# Revit family: ATAG_CV_ketel_Q25_en_Q38_combi
name_source: partatom
category: Mechanical Equipment
revit_build: Autodesk Revit 2014 (Build: 20130308_1515(x64)
units: mm (PartAtom-declared; Revit-internal decimal feet)

## types (2) — shared parameters
BCB_I BaseKeynote = 56.10.10.13.01
BCB_I Beschermingsgraad vlgs. EN 60529 = IPX0D
BCB_I Gaskeur HR Top = HR Top
BCB_I Gaskeur HRww_gaskeurlabel hoog rendement warm water = HR
BCB_I Gaskeur NZ_gaskeurlabel naverwarming zon = NZ
BCB_I Gaskeur SV_gaskeurlabel schone verbranding = SV
BCB_I Max tapwater temperatuur = 60 °C
BCB_V Aansluitdiameter CVr = 28 mm
BCB_V Aansluitdiameter CVv = 28 mm
BCB_V Aansluitdiameter KW = 15 mm
BCB_V Aansluitdiameter WW = 15 mm
BCB_V Aansluitdiameter condensafvoer = 22 mm
BCB_V Aansluitdiameter expansievat = 22 mm
BCB_V Aansluitdiameter gas = 15 mm
BCB_V Aansluitdiameter luchttoevoer = 80 mm  [stored 0.262467 ft]
BCB_V Aansluitdiameter rookgasafvoer = 80 mm  [stored 0.262467 ft]
BCB_V Luchtinlaat_materiaal = BE Kunststof_zwart
BCB_c1 Debiet = 0 CFM
BCB_c1 Omschrijving = c1_Rookgasafvoer
BCB_c1 Straal = 40 mm  [stored 0.131234 ft]
BCB_c10 Omschrijving = c10_Expansievat
BCB_c10 Straal = 11 mm  [stored 0.0360892 ft]
BCB_c2 Omschrijving = c2_Elektrische voeding
BCB_c3 Debiet = 0.0000 L/s
BCB_c3 Energie_inhoud gas = 0 kWh
BCB_c3 Omschrijving = c3_Gasaansluiting
BCB_c3 Straal = 8 mm  [stored 0.0262467 ft]
BCB_c3 Vermogen = 0 kW
BCB_c4 Omschrijving = c4_CV-toevoer
BCB_c4 Straal = 14 mm  [stored 0.0459318 ft]
BCB_c5 Omschrijving = c5_CV-retour
BCB_c5 Straal = 14 mm  [stored 0.0459318 ft]
BCB_c6 Omschrijving = c6_Condensafvoer
BCB_c6 Straal = 11 mm  [stored 0.0360892 ft]
BCB_c7 Debiet = 0 CFM
BCB_c7 Omschrijving = c7_Luchttoevoer
BCB_c7 Straal = 40 mm  [stored 0.131234 ft]
BCB_c8 Debiet = 0.0000 L/s
BCB_c8 Omschrijving = c8_Aansluiting WW
BCB_c8 Straal = 8 mm  [stored 0.0262467 ft]
BCB_c9 Omschrijving = c9_Aansluiting KW
BCB_c9 Straal = 8 mm  [stored 0.0262467 ft]
Default Elevation = 1000 mm  [stored 3.28084 ft]
GTIN-14 = -
IFC_versie = 2x3
IfcExportAs = IfcGasTerminalType
IfcExportType = gasappliance
Manufacturer = ATAG
Model = Q-serie
NL_E Aantal polen = 1
NL_E Arbeidsfactor = 1
NL_E Belastingsklasse = Other
NL_E Belastingssubklasse motor = No
NL_E Schijnbaar vermogen = 0 VA
NL_E Spanning = 230 V
NL_E Vermogen = 0 W
NL_G Breedte = 840 mm
NL_G Diepte = 385 mm  [stored 1.26312 ft]
NL_G Hoogte = 680 mm  [stored 2.23097 ft]
NL_I Bestelcode = -
NL_M Debiet = 0 CFM
NL_P FBW = 0.5
Type Comments = wandketel
ZZ_Z Aansluiting CV_geen accessoire = NL_M Accessoires aansluitingen CV : Geen
ZZ_Z Aansluiting CVr_X coördinaat = -135 mm
ZZ_Z Aansluiting CVr_type accessoire = NL_M Accessoires aansluitingen CV : Kraan
ZZ_Z Aansluiting CVv_X coördinaat = -235 mm
ZZ_Z Aansluiting CVv_type accessoire = NL_M Accessoires aansluitingen CV : Kraan
ZZ_Z Aansluiting KW_X coördinaat = 305 mm
ZZ_Z Aansluiting KW_type accessoire = NL_M Accessoires aansluiting water - kraan : Kraan
ZZ_Z Aansluiting WW_X coördinaat = 375 mm
ZZ_Z Aansluiting WW_type accessoire = NL_M Accessoires aansluiting water - kraan : Kraan
ZZ_Z Aansluiting expansievat_X coördinaat = 10 mm  [stored 0.0328084 ft]
ZZ_Z Aansluiting expansievat_type accessoire = NL_M Accessoires aansluitingen : Geen
ZZ_Z Aansluiting gas_X coördinaat = -355 mm
ZZ_Z Aansluiting gas_geen accessoire = NL_M Accessoires aansluitingen gas : Geen
ZZ_Z Aansluiting gas_type accessoire = NL_M Accessoires aansluitingen gas : Kraan
ZZ_Z Aansluiting luchttoevoer_X coördinaat = 85 mm
ZZ_Z Aansluiting rookgas_X coördinaat = 85 mm
ZZ_Z Aansluiting rookgas_linkerzijde = 335 mm
ZZ_Z Aansluiting water_geen accessoire = NL_M Accessoires aansluiting water - kraan : Geen
ZZ_Z Binnendiameter rookgasafvoer = 60 mm  [stored 0.19685 ft]
ZZ_Z Condensafvoer_X coördinaat = -50 mm
ZZ_Z Condensafvoer_accessoire = NL_M Accessoires aansluitingen CV : Geen
ZZ_Z Halve breedte negatief = -420 mm
fabrikant_artikelcode = -
fabrikant_bibliotheek_versie = v1.0
fabrikant_jaartal = 2014
fabrikant_revisie = -
materiaal = <By Category>
revit_versie = 2014

## per-type parameters (varying)
| type | BCB_I Aantal liters warmwater per minuut (ca. bij 38°C) | BCB_I Aantal liters warmwater per minuut (ca. bij delta T 25°C) | BCB_I Belasting op bovenwaarde CV | BCB_I Belasting op onderwaarde CV | BCB_I Beschikbare opvoerhoogte pomp CV | BCB_I Gasverbruik G25 CV (bij 1013 mbar/15°C)_m3/h | BCB_I Gewicht (leeg) | BCB_I Modulatiebereik CV (vermogen, 50/30°C) | BCB_I Modulatiebereik CV (vermogen, 80/60°C) | BCB_I Rendement volgens EN677 (36/30°C deellast, onderw.) | BCB_I Rendement volgens EN677 (80/60°C vollast, onderw.) |
| Q25C | 13.5000 L/s | 15.0000 L/s | 25000 W | 22500 W | 25000.00 Pa | 2,77 (3,88) | 73 | 6,8 - 23,9 | 6,0 - 21,9 | 109,7 | 97,5 |
| Q38C | 16.6000 L/s | 19.0000 L/s | 38000 W | 34200 W | 20000.00 Pa | 4,21 | 84 | 6,8 - 36,3 | 6,0 - 33,3 | 109,1 | 97,4 |

note: column(s) folded — value = type name in every type: BCB_I Type

note: [stored X ft] marks values corroborated as IEEE doubles in the binary element streams (Revit-internal decimal feet)

## geometry (parser evidence)
native form markers: Blend x2, Sweep x49
no freeform markers — native parametric forms only
